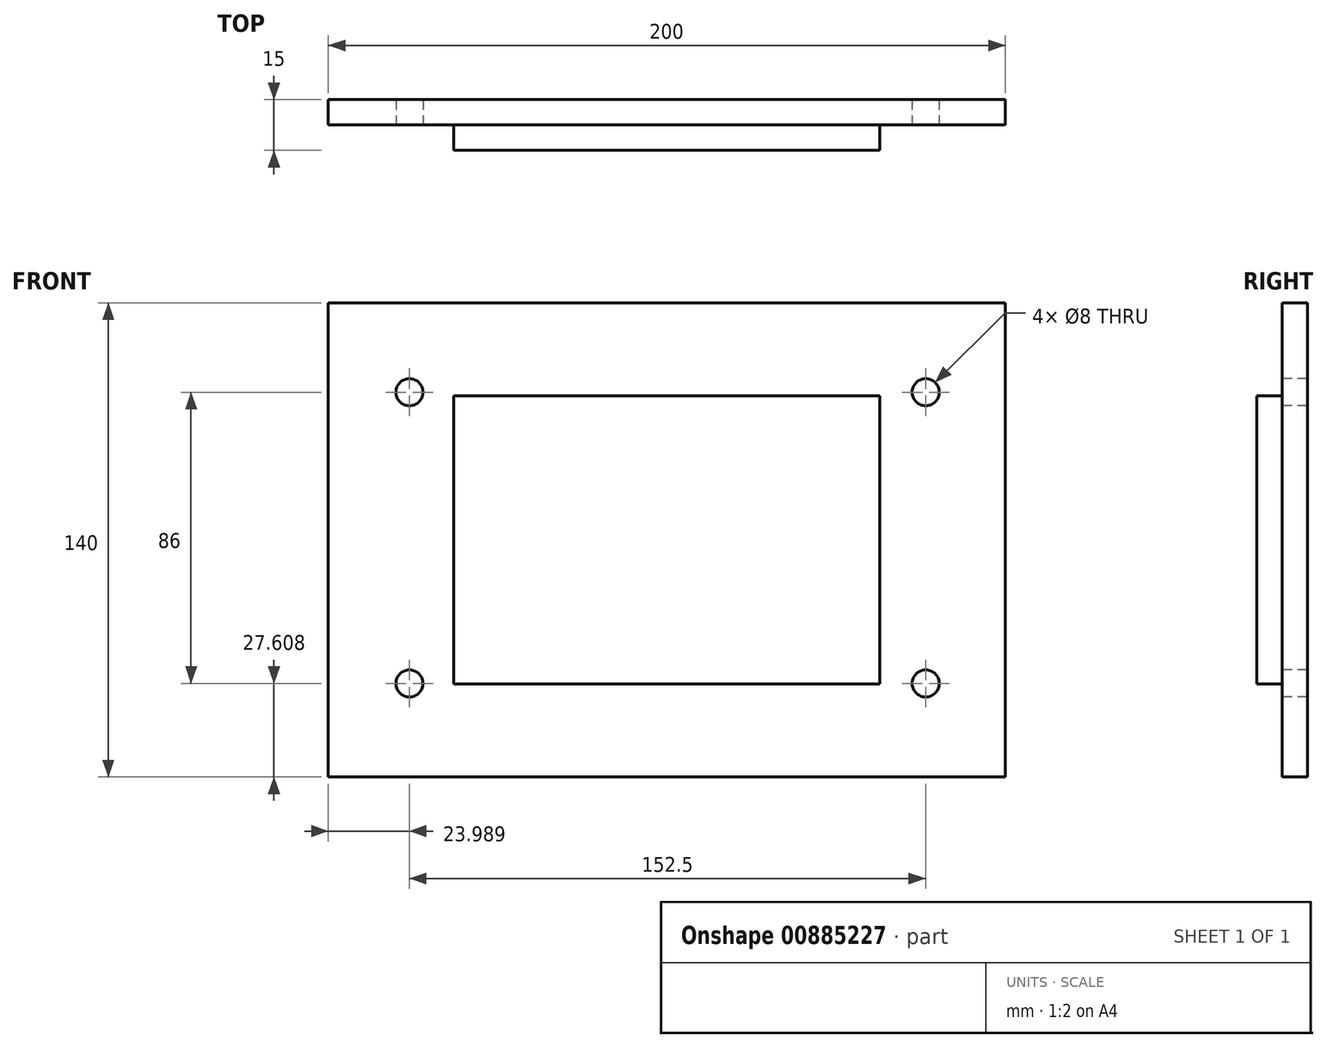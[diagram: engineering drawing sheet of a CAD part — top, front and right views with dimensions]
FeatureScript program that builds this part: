
annotation { "Feature Type Name" : "Feature", "Feature Type Description" : "" }
export const myFeature = defineFeature(function(context is Context, id is Id, definition is map)
    precondition{}
    {
        {
            var Q0;
            Q0=qCreatedBy(makeId("Front.planeOp"),FACE);
            var sketch = newSketch(context, id + "F0", { "sketchPlane" : qUnion([Q0])});
            skLineSegment(sketch, "E0.bottom", {"start": v(-216.17, 134) * mm, "end": v(-16.17, 134) * mm});
            skLineSegment(sketch, "E0.top", {"start": v(-216.17, -6) * mm, "end": v(-16.17, -6) * mm});
            skLineSegment(sketch, "E0.left", {"start": v(-216.17, 134) * mm, "end": v(-216.17, -6) * mm});
            skLineSegment(sketch, "E0.right", {"start": v(-16.17, 134) * mm, "end": v(-16.17, -6) * mm});
            skLineSegment(sketch, "E1.bottom", {"start": v(-179.05, 21.5) * mm, "end": v(-53.3, 21.5) * mm});
            skLineSegment(sketch, "E1.top", {"start": v(-179.05, 106.5) * mm, "end": v(-53.3, 106.5) * mm});
            skLineSegment(sketch, "E1.left", {"start": v(-179.05, 21.5) * mm, "end": v(-179.05, 106.5) * mm});
            skLineSegment(sketch, "E1.right", {"start": v(-53.3, 21.5) * mm, "end": v(-53.3, 106.5) * mm});
            skSolve(sketch);
        }
        {
            var Q0;
            Q0=makeQuery(id+"F0.imprint","IMPRINT",FACE,{"disambiguationData":[TD([[makeQuery(id+"F0.imprint","IMPRINT",EDGE,{"derivedFrom":sQuery(id+"F0.wireOp",EDGE,"E0.bottom")}),-1.0]])]});
            extrude(context, id + "F1", {"entities" : qUnion([Q0]), "depth" : 7.5 * mm, "offsetDistance" : 25 * mm});
        }
        {
            var Q0;
            Q0=makeQuery(id+"F1.opExtrude","CAP_FACE",FACE,{"disambiguationData":[OSD([sQuery(id+"F0.wireOp",EDGE,"E0.bottom"),sQuery(id+"F0.wireOp",EDGE,"E0.top"),sQuery(id+"F0.wireOp",EDGE,"E0.left"),sQuery(id+"F0.wireOp",EDGE,"E0.right")])],"isStart":false});
            var sketch = newSketch(context, id + "F2", { "sketchPlane" : qUnion([Q0])});
            skLineSegment(sketch, "E2", {"start": v(-192.18, 21.6) * mm, "end": v(-39.68, 21.6) * mm});
            skLineSegment(sketch, "E3", {"start": v(-192.18, 21.6) * mm, "end": v(-192.18, 107.6) * mm});
            skLineSegment(sketch, "E4", {"start": v(-192.18, 107.6) * mm, "end": v(-39.68, 107.6) * mm});
            skLineSegment(sketch, "E5", {"start": v(-39.68, 107.6) * mm, "end": v(-39.68, 21.6) * mm});
            skSolve(sketch);
        }
        {
            var Q0;
            Q0=sQuery(id+"F2.wireOp",VERTEX,"E2.end");
            var Q1;
            Q1=sQuery(id+"F2.wireOp",VERTEX,"E2.start");
            var Q2;
            Q2=sQuery(id+"F2.wireOp",VERTEX,"E3.end");
            var Q3;
            Q3=sQuery(id+"F2.wireOp",VERTEX,"E4.end");
            var Q4;
            Q4=makeQuery(id+"F1.opExtrude","SWEPT_BODY",BODY,{"disambiguationData":[OSD([sQuery(id+"F0.wireOp",EDGE,"E0.bottom"),sQuery(id+"F0.wireOp",EDGE,"E0.top"),sQuery(id+"F0.wireOp",EDGE,"E0.left"),sQuery(id+"F0.wireOp",EDGE,"E0.right")])]});
            hole(context, id + "F3", {"style" : HoleStyle.SIMPLE, "endStyle" : HoleEndStyle.BLIND, "holeDiameter" : 8 * mm, "majorDiameter" : 5 * mm, "holeDepth" : 12 * mm, "isTappedThrough" : true, "tappedDepth" : 12 * mm, "tapClearance" : 3, "startFromSketch" : true, "locations" : qUnion([Q0, Q1, Q2, Q3]), "scope" : qUnion([Q4])});
        }
        {
            var Q0;
            Q0=makeQuery(id+"F0.imprint","IMPRINT",FACE,{"disambiguationData":[TD([[makeQuery(id+"F0.imprint","IMPRINT",EDGE,{"derivedFrom":sQuery(id+"F0.wireOp",EDGE,"E1.bottom")}),1.0]])]});
            extrude(context, id + "F4", {"entities" : qUnion([Q0]), "operationType" : NewBodyOperationType.ADD, "depth" : 15 * mm, "offsetDistance" : 25 * mm});
        }
    });
